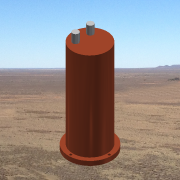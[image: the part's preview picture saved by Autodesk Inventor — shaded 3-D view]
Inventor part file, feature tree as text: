
AUTODESK INVENTOR PART (.ipt)
format: ipt  version: 2014 SP1 (Build 180222100, 222)  size: 165,376 bytes
history: native  units: in
note: dims shown in document units (in); Inventor stores cm internally (conversion verified against a paired STEP export)
features: sketch x5, extrude x4, hole x1, pattern_circular x1
ambient origin geometry x8: Origin, YZ Plane, XZ Plane, XY Plane, X Axis, Y Axis, Z Axis, Center Point
bodies: Solid1 (feature_tree)
feature tree (11):
  extrude  "Extrusion1"  Depth=0.245in
  hole  "Hole1"  [1 undecoded]
  pattern_circular  "Circular Pattern1"  Count=4 Angle=360.0deg
  extrude  "Extrusion2"  Depth=5.4in TaperAngle=0.0deg
  extrude  "Extrusion3"  Depth=0.5in
  extrude  "Extrusion4"  Depth=0.5in
  sketch  "Sketch1"  dims[d0=2.5in d1=0.245in]
  sketch  "Sketch2"  dims[d2=0.25in d3=0.0in d4=1.125in]
  sketch  "Sketch4"  dims[d5=0.132in d6=0.75in d7=0.375in d8=0.25in d9=0.5635in d10=1.0in d11=0.8108in d12=1.5748in d13=360.0deg]
  sketch  "Sketch5"  dims[d16=0.03in d17=5.4in d18=0.0in]
  sketch  "Sketch6"  dims[d19=0.19in d20=0.0in d21=0.41in d22=0.43in d23=0.35in d24=0.5in d25=0.0in]
note: 1 required parameter value undecoded (feature->parameter linkage not recoverable at this tier; creation-order binding heuristic only, values carry confidence <= 0.55)
